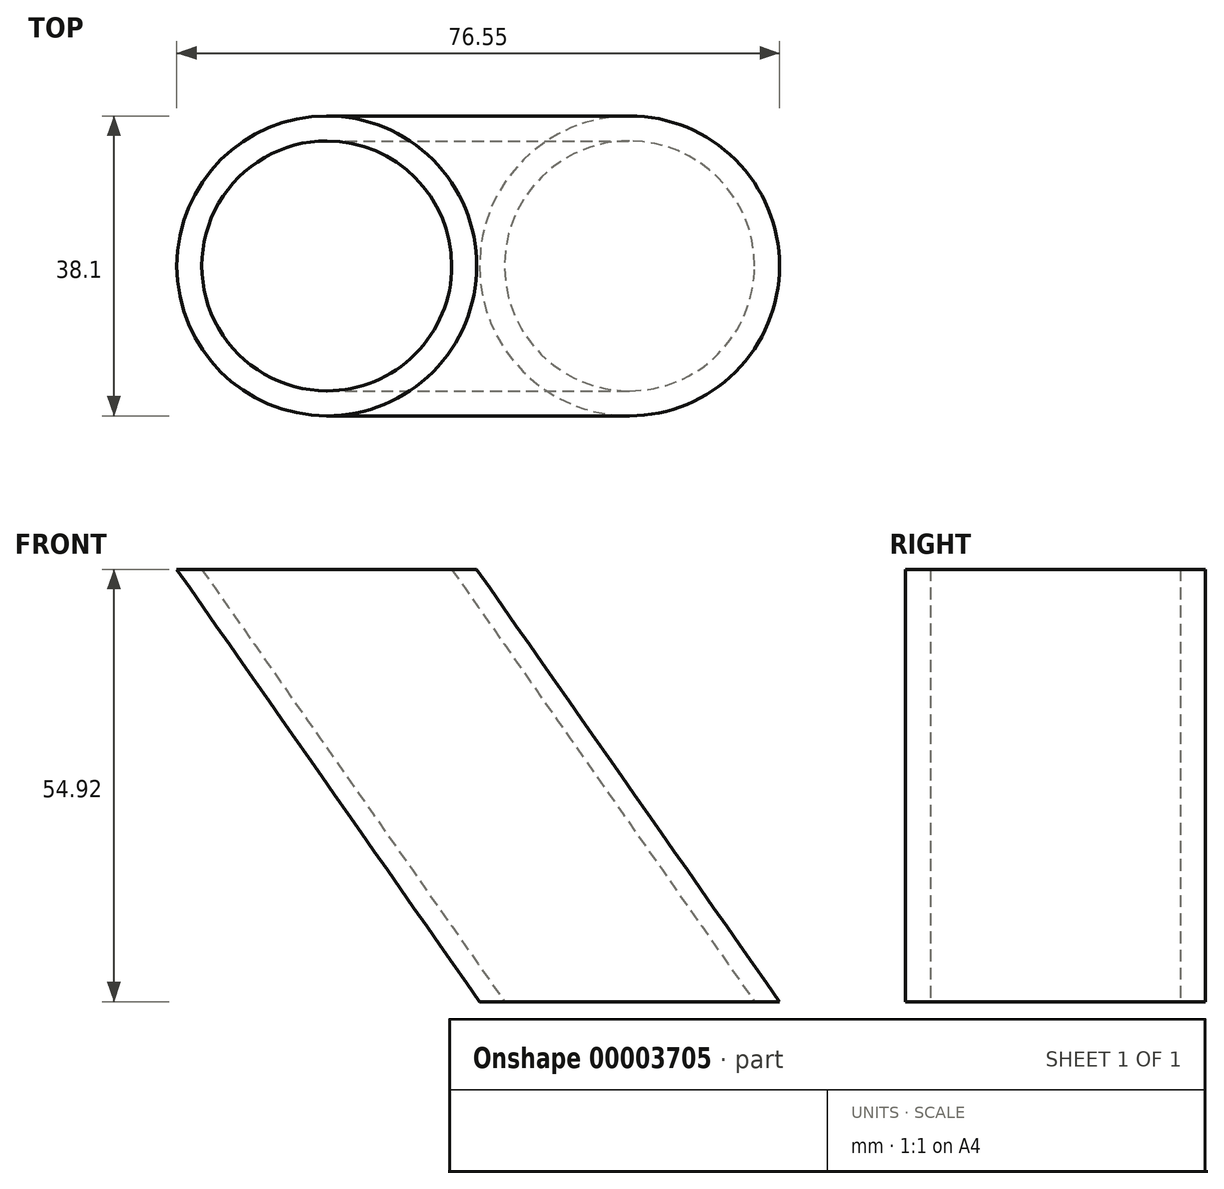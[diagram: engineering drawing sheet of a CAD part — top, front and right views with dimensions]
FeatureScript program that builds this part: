
annotation { "Feature Type Name" : "Feature", "Feature Type Description" : "" }
export const myFeature = defineFeature(function(context is Context, id is Id, definition is map)
    precondition{}
    {
        {
            var Q0;
            Q0=qCreatedBy(makeId("Top.planeOp"),FACE);
            var sketch = newSketch(context, id + "F0", { "sketchPlane" : qUnion([Q0])});
            skCircle(sketch, "E0", {"center": v(0, 0) * mm, "radius": 15.88 * mm});
            skCircle(sketch, "E1", {"center": v(0, 0) * mm, "radius": 19.05 * mm});
            skSolve(sketch);
        }
        {
            var Q0;
            Q0=qCreatedBy(makeId("Front.planeOp"),FACE);
            var sketch = newSketch(context, id + "F1", { "sketchPlane" : qUnion([Q0])});
            skLineSegment(sketch, "E2", {"start": v(0, 0) * mm, "end": v(0, 68.53) * mm, "construction": true});
            skLineSegment(sketch, "E3", {"start": v(0, 0) * mm, "end": v(-38.45, 54.92) * mm});
            skSolve(sketch);
        }
        {
            var Q0;
            Q0=qSketchRegion(id+"F0",true);
            var Q1;
            Q1=sQuery(id+"F1.wireOp",EDGE,"E3");
            sweep(context, id + "F2", {"profiles" : qUnion([Q0]), "path" : qUnion([Q1])});
        }
    });
